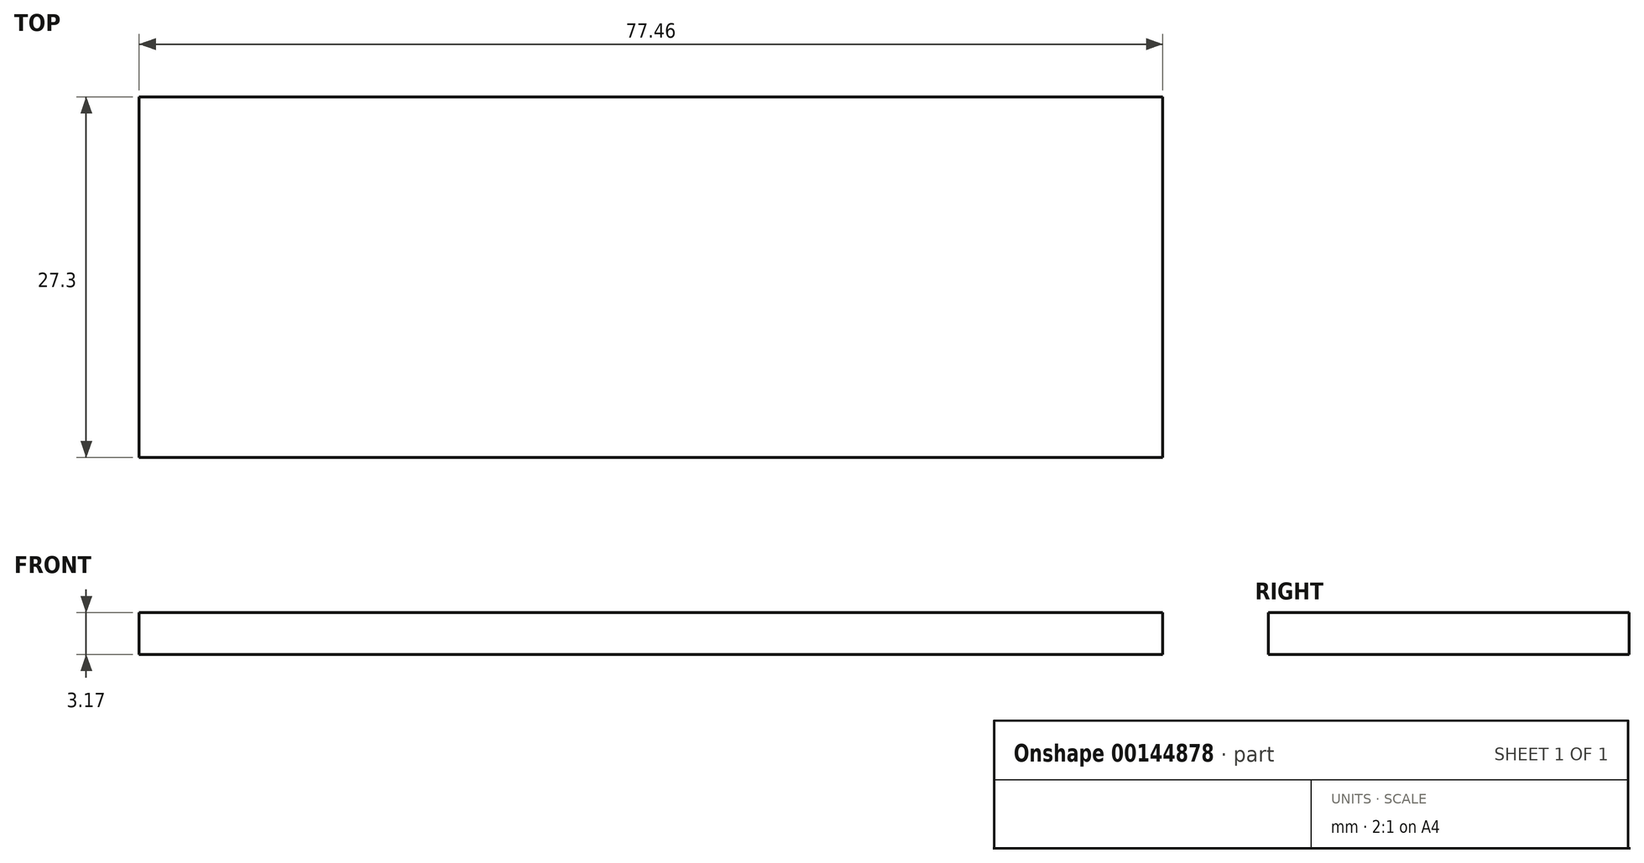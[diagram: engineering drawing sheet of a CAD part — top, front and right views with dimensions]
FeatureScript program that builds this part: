
annotation { "Feature Type Name" : "Feature", "Feature Type Description" : "" }
export const myFeature = defineFeature(function(context is Context, id is Id, definition is map)
    precondition{}
    {
        {
            var Q0;
            Q0=qCreatedBy(makeId("Top.planeOp"),FACE);
            var sketch = newSketch(context, id + "F0", { "sketchPlane" : qUnion([Q0])});
            skLineSegment(sketch, "E0.bottom", {"start": v(-38.73, 13.65) * mm, "end": v(38.73, 13.65) * mm});
            skLineSegment(sketch, "E0.top", {"start": v(-38.73, -13.65) * mm, "end": v(38.73, -13.65) * mm});
            skLineSegment(sketch, "E0.left", {"start": v(-38.73, 13.65) * mm, "end": v(-38.73, -13.65) * mm});
            skLineSegment(sketch, "E0.right", {"start": v(38.73, 13.65) * mm, "end": v(38.73, -13.65) * mm});
            skPoint(sketch, "E0.middle", {"position": v(0, 0) * mm});
            skPoint(sketch, "E1", {"position": v(25.25, 13.65) * mm});
            skPoint(sketch, "E2", {"position": v(-25.25, 13.65) * mm});
            skLineSegment(sketch, "E3.bottom", {"start": v(-25.25, 13.65) * mm, "end": v(-16.61, 13.65) * mm});
            skLineSegment(sketch, "E3.top", {"start": v(-25.25, 16.83) * mm, "end": v(-16.61, 16.83) * mm});
            skLineSegment(sketch, "E3.left", {"start": v(-25.25, 13.65) * mm, "end": v(-25.25, 16.83) * mm});
            skLineSegment(sketch, "E3.right", {"start": v(-16.61, 13.65) * mm, "end": v(-16.61, 16.83) * mm});
            skLineSegment(sketch, "E4.bottom", {"start": v(25.25, 13.65) * mm, "end": v(16.61, 13.65) * mm});
            skLineSegment(sketch, "E4.top", {"start": v(25.25, 16.83) * mm, "end": v(16.61, 16.83) * mm});
            skLineSegment(sketch, "E4.left", {"start": v(25.25, 13.65) * mm, "end": v(25.25, 16.83) * mm});
            skLineSegment(sketch, "E4.right", {"start": v(16.61, 13.65) * mm, "end": v(16.61, 16.83) * mm});
            skLineSegment(sketch, "E5.bottom", {"start": v(-25.25, -13.65) * mm, "end": v(-16.61, -13.65) * mm});
            skLineSegment(sketch, "E5.top", {"start": v(-25.25, -16.83) * mm, "end": v(-16.61, -16.83) * mm});
            skLineSegment(sketch, "E5.left", {"start": v(-25.25, -13.65) * mm, "end": v(-25.25, -16.83) * mm});
            skLineSegment(sketch, "E5.right", {"start": v(-16.61, -13.65) * mm, "end": v(-16.61, -16.83) * mm});
            skPoint(sketch, "E6.oppositeSnap0", {"position": v(25.25, 15.24) * mm});
            skLineSegment(sketch, "E6.bottom", {"start": v(16.61, -13.65) * mm, "end": v(25.25, -13.65) * mm});
            skLineSegment(sketch, "E6.top", {"start": v(16.61, -16.83) * mm, "end": v(25.25, -16.83) * mm});
            skLineSegment(sketch, "E6.left", {"start": v(16.61, -13.65) * mm, "end": v(16.61, -16.83) * mm});
            skLineSegment(sketch, "E6.right", {"start": v(25.25, -13.65) * mm, "end": v(25.25, -16.83) * mm});
            skSolve(sketch);
        }
        {
            var Q0;
            Q0=makeQuery(id+"F0.imprint","IMPRINT",FACE,{"disambiguationData":[TD([[makeQuery(id+"F0.imprint","IMPRINT",EDGE,{"derivedFrom":sQuery(id+"F0.wireOp",EDGE,"E3.bottom")}),1.0]])]});
            var Q1;
            Q1=makeQuery(id+"F0.imprint","IMPRINT",FACE,{"disambiguationData":[TD([[makeQuery(id+"F0.imprint","IMPRINT",EDGE,{"derivedFrom":sQuery(id+"F0.wireOp",EDGE,"E4.bottom")}),-1.0]])]});
            var Q2;
            {var subQ1=sQuery(id+"F0.wireOp",EDGE,"E0.left");Q2=makeQuery(id+"F0.imprint","IMPRINT",FACE,{"disambiguationData":[TD([[makeQuery(id+"F0.imprint","IMPRINT",EDGE,{"derivedFrom":subQ1}),1.0]])]});}
            var Q3;
            Q3=makeQuery(id+"F0.imprint","IMPRINT",FACE,{"disambiguationData":[TD([[makeQuery(id+"F0.imprint","IMPRINT",EDGE,{"derivedFrom":sQuery(id+"F0.wireOp",EDGE,"E5.bottom")}),-1.0]])]});
            var Q4;
            Q4=makeQuery(id+"F0.imprint","IMPRINT",FACE,{"disambiguationData":[TD([[makeQuery(id+"F0.imprint","IMPRINT",EDGE,{"derivedFrom":sQuery(id+"F0.wireOp",EDGE,"E6.bottom")}),-1.0]])]});
            extrude(context, id + "F1", {"entities" : qUnion([Q0, Q1, Q2, Q3, Q4]), "depth" : 3.17 * mm});
        }
    });
